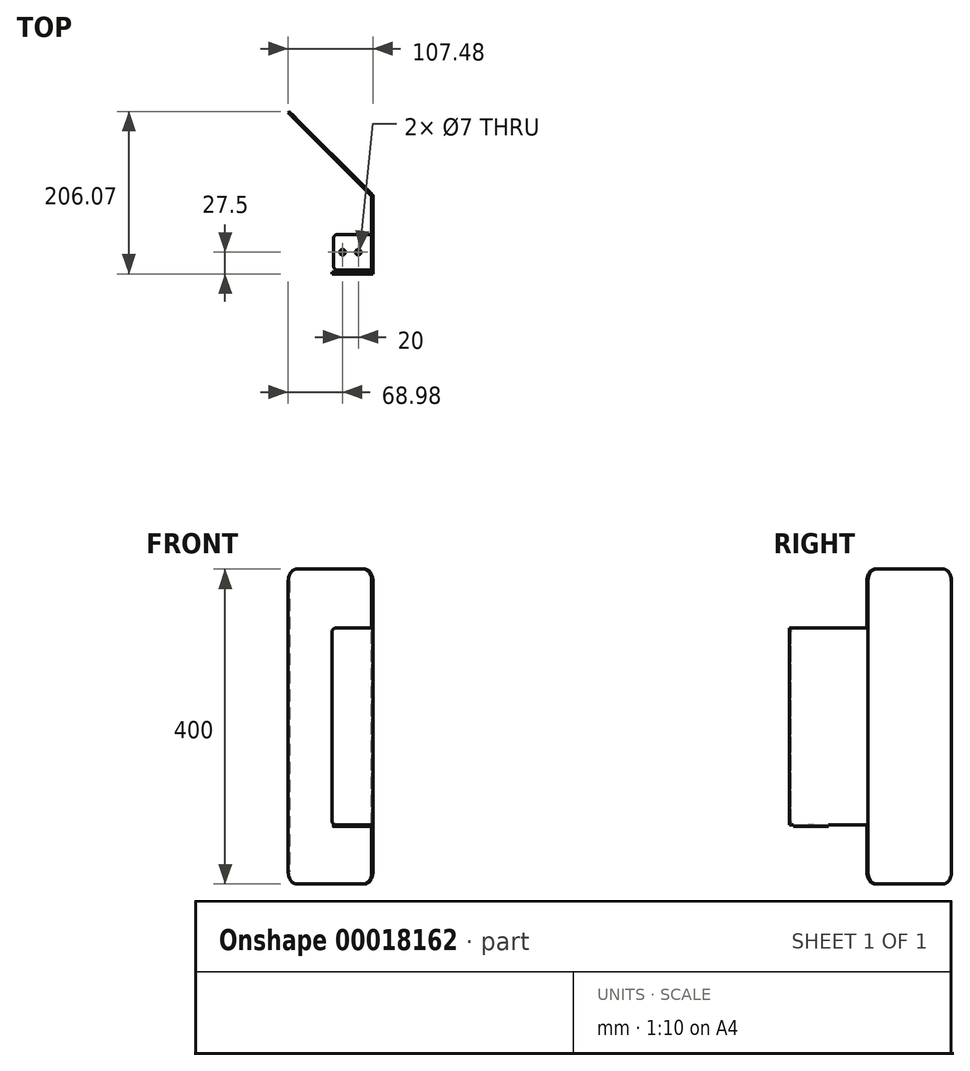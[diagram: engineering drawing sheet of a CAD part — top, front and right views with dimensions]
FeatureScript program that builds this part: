
annotation { "Feature Type Name" : "Feature", "Feature Type Description" : "" }
export const myFeature = defineFeature(function(context is Context, id is Id, definition is map)
    precondition{}
    {
        {
            var Q0;
            Q0=qCreatedBy(makeId("Front.planeOp"),FACE);
            var sketch = newSketch(context, id + "F0", { "sketchPlane" : qUnion([Q0])});
            skLineSegment(sketch, "E0.bottom", {"start": v(0, -125) * mm, "end": v(-45, -125) * mm});
            skLineSegment(sketch, "E0.top", {"start": v(0, 125) * mm, "end": v(-45, 125) * mm});
            skLineSegment(sketch, "E0.left", {"start": v(0, -125) * mm, "end": v(0, 125) * mm});
            skLineSegment(sketch, "E0.right", {"start": v(-50, -120) * mm, "end": v(-50, 120) * mm});
            skLineSegment(sketch, "E1", {"start": v(0, 0) * mm, "end": v(-144.9, 0) * mm, "construction": true});
            skPoint(sketch, "E2.visualSharp", {"position": v(-50, 125) * mm});
            skArc(sketch, "E2.filletArc", {"start": v(-45, 125) * mm, "mid": v(-48.54, 123.54) * mm, "end": v(-50, 120) * mm});
            skPoint(sketch, "E3.visualSharp", {"position": v(-50, -125) * mm});
            skArc(sketch, "E3.filletArc", {"start": v(-50, -120) * mm, "mid": v(-48.54, -123.54) * mm, "end": v(-45, -125) * mm});
            skSolve(sketch);
        }
        {
            var Q0;
            Q0=qSketchRegion(id+"F0",true);
            extrude(context, id + "F1", {"entities" : qUnion([Q0]), "depth" : 2 * mm});
        }
        {
            var Q0;
            Q0=makeQuery(id+"F1.opExtrude","SWEPT_FACE",FACE,{"disambiguationData":[OSD([sQuery(id+"F0.wireOp",EDGE,"E0.left")])]});
            var sketch = newSketch(context, id + "F2", { "sketchPlane" : qUnion([Q0])});
            skLineSegment(sketch, "E4.bottom", {"start": v(-2, 125) * mm, "end": v(98, 125) * mm});
            skLineSegment(sketch, "E4.top", {"start": v(-2, -125) * mm, "end": v(98, -125) * mm});
            skLineSegment(sketch, "E4.left", {"start": v(-2, 125) * mm, "end": v(-2, -125) * mm});
            skLineSegment(sketch, "E4.right", {"start": v(98, 125) * mm, "end": v(98, -125) * mm});
            skSolve(sketch);
        }
        {
            var Q0;
            Q0=qSketchRegion(id+"F2",true);
            extrude(context, id + "F3", {"entities" : qUnion([Q0]), "operationType" : NewBodyOperationType.ADD, "depth" : 2 * mm});
        }
        {
            var Q0;
            Q0=makeQuery(id+"F3.opExtrude","CAP_EDGE",EDGE,{"disambiguationData":[OSD([sQuery(id+"F2.wireOp",EDGE,"E4.right")])],"isStart":false});
            cPlane(context, id + "F4", {"entities" : qUnion([Q0]), "cplaneType" : CPlaneType.LINE_ANGLE, "offset" : 152.4 * mm, "angle" : 135 * degree, "width" : 152.4 * mm, "height" : 152.4 * mm});
        }
        {
            var Q0;
            Q0=qCreatedBy(id+"F4.planeOp",FACE);
            var sketch = newSketch(context, id + "F5", { "sketchPlane" : qUnion([Q0])});
            skLineSegment(sketch, "E5.bottom", {"start": v(82.88, 200) * mm, "end": v(202.88, 200) * mm});
            skLineSegment(sketch, "E5.top", {"start": v(82.88, -200) * mm, "end": v(202.88, -200) * mm});
            skLineSegment(sketch, "E5.left", {"start": v(67.88, 185) * mm, "end": v(67.88, -185) * mm});
            skLineSegment(sketch, "E5.right", {"start": v(217.88, 185) * mm, "end": v(217.88, -185) * mm});
            skPoint(sketch, "E6.visualSharp", {"position": v(67.88, 200) * mm});
            skArc(sketch, "E6.filletArc", {"start": v(82.88, 200) * mm, "mid": v(72.28, 195.6) * mm, "end": v(67.88, 185) * mm});
            skPoint(sketch, "E7.visualSharp", {"position": v(217.88, 200) * mm});
            skArc(sketch, "E7.filletArc", {"start": v(217.88, 185) * mm, "mid": v(213.49, 195.6) * mm, "end": v(202.88, 200) * mm});
            skPoint(sketch, "E8.visualSharp", {"position": v(217.88, -200) * mm});
            skArc(sketch, "E8.filletArc", {"start": v(202.88, -200) * mm, "mid": v(213.49, -195.6) * mm, "end": v(217.88, -185) * mm});
            skPoint(sketch, "E9.visualSharp", {"position": v(67.88, -200) * mm});
            skArc(sketch, "E9.filletArc", {"start": v(67.88, -185) * mm, "mid": v(72.28, -195.6) * mm, "end": v(82.88, -200) * mm});
            skSolve(sketch);
        }
        {
            var Q0;
            Q0=qSketchRegion(id+"F5",true);
            extrude(context, id + "F6", {"entities" : qUnion([Q0]), "oppositeDirection" : true, "depth" : 2 * mm});
        }
        {
            var Q0;
            Q0=makeQuery(id+"F3.boolean.opBoolean","MERGE",FACE,{"derivedFrom":[makeQuery(id+"F1.opExtrude","SWEPT_FACE",FACE,{"disambiguationData":[OSD([sQuery(id+"F0.wireOp",EDGE,"E0.bottom")])]}),makeQuery(id+"F3.opExtrude","SWEPT_FACE",FACE,{"disambiguationData":[OSD([sQuery(id+"F2.wireOp",EDGE,"E4.top")])]})]});
            var sketch = newSketch(context, id + "F7", { "sketchPlane" : qUnion([Q0])});
            skLineSegment(sketch, "E10.bottom", {"start": v(2, -3) * mm, "end": v(-43, -3) * mm});
            skLineSegment(sketch, "E10.top", {"start": v(2, -48) * mm, "end": v(-43, -48) * mm});
            skLineSegment(sketch, "E10.left", {"start": v(2, -3) * mm, "end": v(2, -48) * mm});
            skLineSegment(sketch, "E10.right", {"start": v(-48, -8) * mm, "end": v(-48, -43) * mm});
            skPoint(sketch, "E11.visualSharp", {"position": v(-48, -3) * mm});
            skArc(sketch, "E11.filletArc", {"start": v(-43, -3) * mm, "mid": v(-46.54, -4.46) * mm, "end": v(-48, -8) * mm});
            skPoint(sketch, "E12.visualSharp", {"position": v(-48, -48) * mm});
            skArc(sketch, "E12.filletArc", {"start": v(-48, -43) * mm, "mid": v(-46.54, -46.54) * mm, "end": v(-43, -48) * mm});
            skCircle(sketch, "E13", {"center": v(-16.5, -25.5) * mm, "radius": 3.5 * mm});
            skCircle(sketch, "E14", {"center": v(-36.5, -25.5) * mm, "radius": 3.5 * mm});
            skLineSegment(sketch, "E15", {"start": v(-48, -25.5) * mm, "end": v(-7.46, -25.5) * mm, "construction": true});
            skSolve(sketch);
        }
        {
            var Q0;
            Q0=qSketchRegion(id+"F7",true);
            extrude(context, id + "F8", {"entities" : qUnion([Q0]), "operationType" : NewBodyOperationType.ADD, "depth" : 2 * mm});
        }
    });
